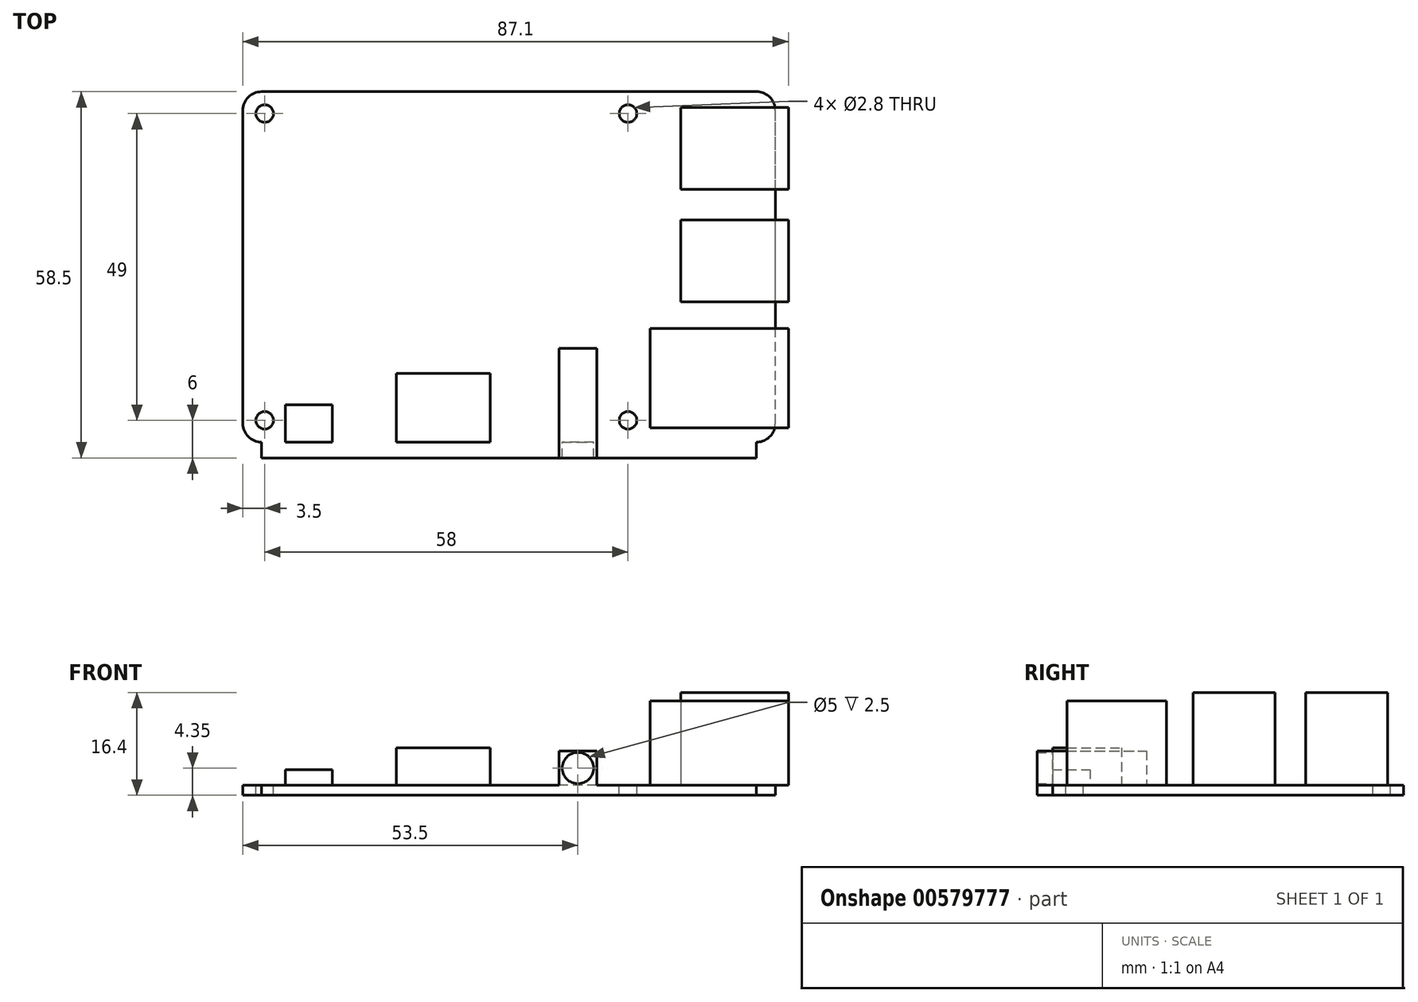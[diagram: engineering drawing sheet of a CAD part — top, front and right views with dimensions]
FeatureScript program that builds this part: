
annotation { "Feature Type Name" : "Feature", "Feature Type Description" : "" }
export const myFeature = defineFeature(function(context is Context, id is Id, definition is map)
    precondition{}
    {
        {
            var Q0;
            Q0=qCreatedBy(makeId("Top.planeOp"),FACE);
            var sketch = newSketch(context, id + "F0", { "sketchPlane" : qUnion([Q0])});
            skLineSegment(sketch, "E0", {"start": v(3, 0) * mm, "end": v(82, 0) * mm});
            skLineSegment(sketch, "E1", {"start": v(85, 3) * mm, "end": v(85, 53) * mm});
            skLineSegment(sketch, "E2", {"start": v(82, 56) * mm, "end": v(3, 56) * mm});
            skLineSegment(sketch, "E3", {"start": v(0, 53) * mm, "end": v(0, 3) * mm});
            skPoint(sketch, "E4.visualSharp", {"position": v(0, 56) * mm});
            skArc(sketch, "E4.filletArc", {"start": v(3, 56) * mm, "mid": v(0.88, 55.12) * mm, "end": v(0, 53) * mm});
            skPoint(sketch, "E5.visualSharp", {"position": v(0, 0) * mm});
            skArc(sketch, "E5.filletArc", {"start": v(0, 3) * mm, "mid": v(0.88, 0.88) * mm, "end": v(3, 0) * mm});
            skPoint(sketch, "E6.visualSharp", {"position": v(85, 0) * mm});
            skArc(sketch, "E6.filletArc", {"start": v(82, 0) * mm, "mid": v(84.12, 0.88) * mm, "end": v(85, 3) * mm});
            skPoint(sketch, "E7.visualSharp", {"position": v(85, 56) * mm});
            skArc(sketch, "E7.filletArc", {"start": v(85, 53) * mm, "mid": v(84.12, 55.12) * mm, "end": v(82, 56) * mm});
            skCircle(sketch, "E8", {"center": v(3.5, 52.5) * mm, "radius": 1.4 * mm});
            skCircle(sketch, "E9", {"center": v(61.5, 52.5) * mm, "radius": 1.4 * mm});
            skCircle(sketch, "E10", {"center": v(61.5, 3.5) * mm, "radius": 1.4 * mm});
            skCircle(sketch, "E11", {"center": v(3.5, 3.5) * mm, "radius": 1.4 * mm});
            skSolve(sketch);
        }
        {
            var Q0;
            Q0=makeQuery(id+"F0.imprint","IMPRINT",FACE,{"disambiguationData":[TD([[makeQuery(id+"F0.imprint","IMPRINT",EDGE,{"derivedFrom":sQuery(id+"F0.wireOp",EDGE,"E0")}),1.0]])]});
            extrude(context, id + "F1", {"entities" : qUnion([Q0]), "oppositeDirection" : true, "depth" : 1.6 * mm, "offsetDistance" : 25 * mm});
        }
        {
            var Q0;
            Q0=makeQuery(id+"F1.opExtrude","CAP_FACE",FACE,{"disambiguationData":[OSD([sQuery(id+"F0.wireOp",EDGE,"E0"),sQuery(id+"F0.wireOp",EDGE,"E1"),sQuery(id+"F0.wireOp",EDGE,"E2"),sQuery(id+"F0.wireOp",EDGE,"E3"),sQuery(id+"F0.wireOp",EDGE,"E4.filletArc"),sQuery(id+"F0.wireOp",EDGE,"E5.filletArc"),sQuery(id+"F0.wireOp",EDGE,"E6.filletArc"),sQuery(id+"F0.wireOp",EDGE,"E7.filletArc"),sQuery(id+"F0.wireOp",EDGE,"E8"),sQuery(id+"F0.wireOp",EDGE,"E9"),sQuery(id+"F0.wireOp",EDGE,"E10"),sQuery(id+"F0.wireOp",EDGE,"E11")])],"isStart":true});
            var sketch = newSketch(context, id + "F2", { "sketchPlane" : qUnion([Q0])});
            skLineSegment(sketch, "E12", {"start": v(87.1, 2.3) * mm, "end": v(87.1, 18.2) * mm});
            skLineSegment(sketch, "E13", {"start": v(65, 18.2) * mm, "end": v(65, 2.3) * mm});
            skLineSegment(sketch, "E14", {"start": v(65, 2.3) * mm, "end": v(87.1, 2.3) * mm});
            skLineSegment(sketch, "E15", {"start": v(87.1, 18.2) * mm, "end": v(65, 18.2) * mm});
            skSolve(sketch);
        }
        {
            var Q0;
            {var subQ5=sQuery(id+"F2.wireOp",EDGE,"E12");Q0=makeQuery(id+"F2.imprint","IMPRINT",FACE,{"disambiguationData":[TD([[makeQuery(id+"F2.imprint","IMPRINT",EDGE,{"derivedFrom":subQ5}),1.0]])]});}
            var Q1;
            {var subQ1=sQuery(id+"F2.wireOp",EDGE,"E13");Q1=makeQuery(id+"F2.imprint","IMPRINT",FACE,{"disambiguationData":[TD([[makeQuery(id+"F2.imprint","IMPRINT",EDGE,{"derivedFrom":subQ1}),1.0]])]});}
            extrude(context, id + "F3", {"entities" : qUnion([Q0, Q1]), "operationType" : NewBodyOperationType.ADD, "depth" : 13.5 * mm, "offsetDistance" : 25 * mm});
        }
        {
            var Q0;
            Q0=makeQuery(id+"F1.opExtrude","CAP_FACE",FACE,{"disambiguationData":[OSD([sQuery(id+"F0.wireOp",EDGE,"E0"),sQuery(id+"F0.wireOp",EDGE,"E1"),sQuery(id+"F0.wireOp",EDGE,"E2"),sQuery(id+"F0.wireOp",EDGE,"E3"),sQuery(id+"F0.wireOp",EDGE,"E4.filletArc"),sQuery(id+"F0.wireOp",EDGE,"E5.filletArc"),sQuery(id+"F0.wireOp",EDGE,"E6.filletArc"),sQuery(id+"F0.wireOp",EDGE,"E7.filletArc"),sQuery(id+"F0.wireOp",EDGE,"E8"),sQuery(id+"F0.wireOp",EDGE,"E9"),sQuery(id+"F0.wireOp",EDGE,"E10"),sQuery(id+"F0.wireOp",EDGE,"E11")])],"isStart":true});
            var sketch = newSketch(context, id + "F4", { "sketchPlane" : qUnion([Q0])});
            skLineSegment(sketch, "E16.bottom", {"start": v(69.9, 53.5) * mm, "end": v(87.1, 53.5) * mm});
            skLineSegment(sketch, "E16.top", {"start": v(69.9, 40.4) * mm, "end": v(87.1, 40.4) * mm});
            skLineSegment(sketch, "E16.left", {"start": v(69.9, 53.5) * mm, "end": v(69.9, 40.4) * mm});
            skLineSegment(sketch, "E16.right", {"start": v(87.1, 53.5) * mm, "end": v(87.1, 40.4) * mm});
            skLineSegment(sketch, "E17.bottom", {"start": v(69.9, 35.5) * mm, "end": v(87.1, 35.5) * mm});
            skLineSegment(sketch, "E17.top", {"start": v(69.9, 22.4) * mm, "end": v(87.1, 22.4) * mm});
            skLineSegment(sketch, "E17.left", {"start": v(69.9, 35.5) * mm, "end": v(69.9, 22.4) * mm});
            skLineSegment(sketch, "E17.right", {"start": v(87.1, 35.5) * mm, "end": v(87.1, 22.4) * mm});
            skSolve(sketch);
        }
        {
            var Q0;
            {var subQ0=sQuery(id+"F4.wireOp",EDGE,"E17.left");Q0=makeQuery(id+"F4.imprint","IMPRINT",FACE,{"disambiguationData":[TD([[makeQuery(id+"F4.imprint","IMPRINT",EDGE,{"derivedFrom":subQ0}),1.0]])]});}
            var Q1;
            {var subQ7=sQuery(id+"F4.wireOp",EDGE,"E16.left");Q1=makeQuery(id+"F4.imprint","IMPRINT",FACE,{"disambiguationData":[TD([[makeQuery(id+"F4.imprint","IMPRINT",EDGE,{"derivedFrom":subQ7}),1.0]])]});}
            var Q2;
            {var subQ0=sQuery(id+"F4.wireOp",EDGE,"E16.right");Q2=makeQuery(id+"F4.imprint","IMPRINT",FACE,{"disambiguationData":[TD([[makeQuery(id+"F4.imprint","IMPRINT",EDGE,{"derivedFrom":subQ0}),-1.0]])]});}
            var Q3;
            {var subQ0=sQuery(id+"F4.wireOp",EDGE,"E17.right");Q3=makeQuery(id+"F4.imprint","IMPRINT",FACE,{"disambiguationData":[TD([[makeQuery(id+"F4.imprint","IMPRINT",EDGE,{"derivedFrom":subQ0}),-1.0]])]});}
            extrude(context, id + "F5", {"entities" : qUnion([Q0, Q1, Q2, Q3]), "operationType" : NewBodyOperationType.ADD, "depth" : 14.8 * mm, "offsetDistance" : 25 * mm});
        }
        {
            var Q0;
            Q0=makeQuery(id+"F1.opExtrude","CAP_FACE",FACE,{"disambiguationData":[OSD([sQuery(id+"F0.wireOp",EDGE,"E0"),sQuery(id+"F0.wireOp",EDGE,"E1"),sQuery(id+"F0.wireOp",EDGE,"E2"),sQuery(id+"F0.wireOp",EDGE,"E3"),sQuery(id+"F0.wireOp",EDGE,"E4.filletArc"),sQuery(id+"F0.wireOp",EDGE,"E5.filletArc"),sQuery(id+"F0.wireOp",EDGE,"E6.filletArc"),sQuery(id+"F0.wireOp",EDGE,"E7.filletArc"),sQuery(id+"F0.wireOp",EDGE,"E8"),sQuery(id+"F0.wireOp",EDGE,"E9"),sQuery(id+"F0.wireOp",EDGE,"E10"),sQuery(id+"F0.wireOp",EDGE,"E11")])],"isStart":true});
            var sketch = newSketch(context, id + "F6", { "sketchPlane" : qUnion([Q0])});
            skLineSegment(sketch, "E18.bottom", {"start": v(56.5, 0) * mm, "end": v(50.5, 0) * mm});
            skLineSegment(sketch, "E18.top", {"start": v(56.5, 15) * mm, "end": v(50.5, 15) * mm});
            skLineSegment(sketch, "E18.left", {"start": v(56.5, 0) * mm, "end": v(56.5, 15) * mm});
            skLineSegment(sketch, "E18.right", {"start": v(50.5, 0) * mm, "end": v(50.5, 15) * mm});
            skSolve(sketch);
        }
        {
            var Q0;
            Q0=makeQuery(id+"F6.imprint","IMPRINT",FACE,{"disambiguationData":[TD([[makeQuery(id+"F6.imprint","IMPRINT",EDGE,{"derivedFrom":sQuery(id+"F6.wireOp",EDGE,"E18.bottom")}),1.0]])]});
            extrude(context, id + "F7", {"entities" : qUnion([Q0]), "operationType" : NewBodyOperationType.ADD, "depth" : 5.5 * mm, "offsetDistance" : 25 * mm});
        }
        {
            var Q0;
            Q0=makeQuery(id+"F7.boolean.opBoolean","MERGE",FACE,{"derivedFrom":[makeQuery(id+"F1.opExtrude","SWEPT_FACE",FACE,{"disambiguationData":[OSD([sQuery(id+"F0.wireOp",EDGE,"E0")])]}),makeQuery(id+"F7.opExtrude","SWEPT_FACE",FACE,{"disambiguationData":[OSD([sQuery(id+"F6.wireOp",EDGE,"E18.bottom")])]})]});
            var sketch = newSketch(context, id + "F8", { "sketchPlane" : qUnion([Q0])});
            skLineSegment(sketch, "E19", {"start": v(50.5, 5.5) * mm, "end": v(56.5, 0) * mm});
            skCircle(sketch, "E20", {"center": v(53.5, 2.75) * mm, "radius": 2.5 * mm});
            skSolve(sketch);
        }
        {
            var Q0;
            {var subQ0=sQuery(id+"F8.wireOp",EDGE,"E20");var subQ1=sQuery(id+"F8.wireOp",EDGE,"E19");var subQ2=makeQuery(id+"F8.imprint","INTERSECT",VERTEX,{"disambiguationData":[OD(0.0)],"derivedFrom":[subQ1,subQ0]});Q0=makeQuery(id+"F8.imprint","IMPRINT",FACE,{"disambiguationData":[TD([[makeQuery(id+"F8.imprint","IMPRINT",EDGE,{"disambiguationData":[TD([[subQ2,-1.0]])],"derivedFrom":subQ1}),-1.0]])]});}
            var Q1;
            {var subQ0=sQuery(id+"F8.wireOp",EDGE,"E20");var subQ1=sQuery(id+"F8.wireOp",EDGE,"E19");var subQ2=makeQuery(id+"F8.imprint","INTERSECT",VERTEX,{"disambiguationData":[OD(0.0)],"derivedFrom":[subQ1,subQ0]});Q1=makeQuery(id+"F8.imprint","IMPRINT",FACE,{"disambiguationData":[TD([[makeQuery(id+"F8.imprint","IMPRINT",EDGE,{"disambiguationData":[TD([[subQ2,-1.0]])],"derivedFrom":subQ1}),1.0]])]});}
            extrude(context, id + "F9", {"entities" : qUnion([Q0, Q1]), "operationType" : NewBodyOperationType.ADD, "depth" : 2.5 * mm, "offsetDistance" : 25 * mm});
        }
        {
            var Q0;
            Q0=makeQuery(id+"F1.opExtrude","CAP_FACE",FACE,{"disambiguationData":[OSD([sQuery(id+"F0.wireOp",EDGE,"E0"),sQuery(id+"F0.wireOp",EDGE,"E1"),sQuery(id+"F0.wireOp",EDGE,"E2"),sQuery(id+"F0.wireOp",EDGE,"E3"),sQuery(id+"F0.wireOp",EDGE,"E4.filletArc"),sQuery(id+"F0.wireOp",EDGE,"E5.filletArc"),sQuery(id+"F0.wireOp",EDGE,"E6.filletArc"),sQuery(id+"F0.wireOp",EDGE,"E7.filletArc"),sQuery(id+"F0.wireOp",EDGE,"E8"),sQuery(id+"F0.wireOp",EDGE,"E9"),sQuery(id+"F0.wireOp",EDGE,"E10"),sQuery(id+"F0.wireOp",EDGE,"E11")])],"isStart":true});
            var sketch = newSketch(context, id + "F10", { "sketchPlane" : qUnion([Q0])});
            skLineSegment(sketch, "E21.bottom", {"start": v(24.5, 0) * mm, "end": v(39.5, 0) * mm});
            skLineSegment(sketch, "E21.top", {"start": v(24.5, 11) * mm, "end": v(39.5, 11) * mm});
            skLineSegment(sketch, "E21.left", {"start": v(24.5, 0) * mm, "end": v(24.5, 11) * mm});
            skLineSegment(sketch, "E21.right", {"start": v(39.5, 0) * mm, "end": v(39.5, 11) * mm});
            skSolve(sketch);
        }
        {
            var Q0;
            Q0=makeQuery(id+"F10.imprint","IMPRINT",FACE,{"disambiguationData":[TD([[makeQuery(id+"F10.imprint","IMPRINT",EDGE,{"derivedFrom":sQuery(id+"F10.wireOp",EDGE,"E21.bottom")}),1.0]])]});
            extrude(context, id + "F11", {"entities" : qUnion([Q0]), "operationType" : NewBodyOperationType.ADD, "depth" : 6 * mm, "offsetDistance" : 25 * mm});
        }
        {
            var Q0;
            Q0=makeQuery(id+"F1.opExtrude","CAP_FACE",FACE,{"disambiguationData":[OSD([sQuery(id+"F0.wireOp",EDGE,"E0"),sQuery(id+"F0.wireOp",EDGE,"E1"),sQuery(id+"F0.wireOp",EDGE,"E2"),sQuery(id+"F0.wireOp",EDGE,"E3"),sQuery(id+"F0.wireOp",EDGE,"E4.filletArc"),sQuery(id+"F0.wireOp",EDGE,"E5.filletArc"),sQuery(id+"F0.wireOp",EDGE,"E6.filletArc"),sQuery(id+"F0.wireOp",EDGE,"E7.filletArc"),sQuery(id+"F0.wireOp",EDGE,"E8"),sQuery(id+"F0.wireOp",EDGE,"E9"),sQuery(id+"F0.wireOp",EDGE,"E10"),sQuery(id+"F0.wireOp",EDGE,"E11")])],"isStart":true});
            var sketch = newSketch(context, id + "F12", { "sketchPlane" : qUnion([Q0])});
            skLineSegment(sketch, "E22.bottom", {"start": v(6.8, 0) * mm, "end": v(14.3, 0) * mm});
            skLineSegment(sketch, "E22.top", {"start": v(6.8, 6) * mm, "end": v(14.3, 6) * mm});
            skLineSegment(sketch, "E22.left", {"start": v(6.8, 0) * mm, "end": v(6.8, 6) * mm});
            skLineSegment(sketch, "E22.right", {"start": v(14.3, 0) * mm, "end": v(14.3, 6) * mm});
            skSolve(sketch);
        }
        {
            var Q0;
            Q0=makeQuery(id+"F12.imprint","IMPRINT",FACE,{"disambiguationData":[TD([[makeQuery(id+"F12.imprint","IMPRINT",EDGE,{"derivedFrom":sQuery(id+"F12.wireOp",EDGE,"E22.bottom")}),1.0]])]});
            extrude(context, id + "F13", {"entities" : qUnion([Q0]), "operationType" : NewBodyOperationType.ADD, "depth" : 2.5 * mm, "offsetDistance" : 25 * mm});
        }
    });
